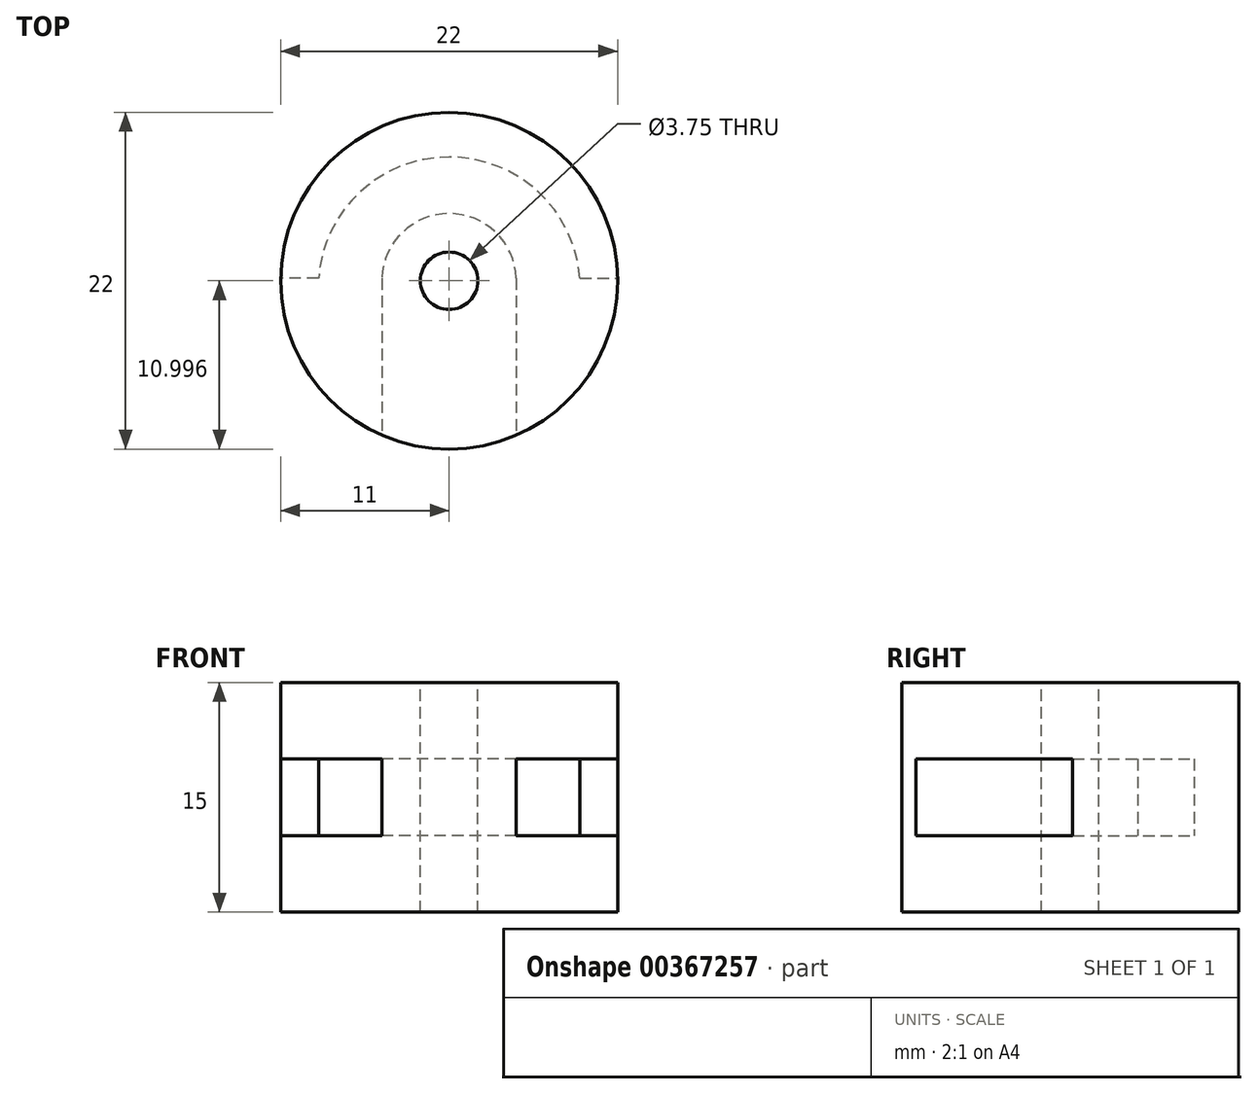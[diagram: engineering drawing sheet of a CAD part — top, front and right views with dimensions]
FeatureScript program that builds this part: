
annotation { "Feature Type Name" : "Feature", "Feature Type Description" : "" }
export const myFeature = defineFeature(function(context is Context, id is Id, definition is map)
    precondition{}
    {
        {
            var Q0;
            Q0=qCreatedBy(makeId("Top.planeOp"),FACE);
            var sketch = newSketch(context, id + "F0", { "sketchPlane" : qUnion([Q0])});
            skCircle(sketch, "E0", {"center": v(-55.33, -34.02) * mm, "radius": 11 * mm});
            skSolve(sketch);
        }
        {
            var Q0;
            Q0 = qSketchRegion(id + "F0", true);
            extrude(context, id + "F1", {"entities" : qUnion([Q0]), "depth" : 5 * mm});
        }
        {
            var Q0;
            Q0=makeQuery(id+"F1.opExtrude","CAP_FACE",FACE,{"disambiguationData":[OSD([sQuery(id+"F0.wireOp",EDGE,"E0")])],"isStart":false});
            var sketch = newSketch(context, id + "F2", { "sketchPlane" : qUnion([Q0])});
            skCircle(sketch, "E1", {"center": v(-55.33, -34.02) * mm, "radius": 11 * mm});
            skCircle(sketch, "E2", {"center": v(-55.33, -34.02) * mm, "radius": 1.88 * mm, "construction": true});
            skArc(sketch, "E3", {"start": v(-50.94, -34.18) * mm, "mid": v(-55.33, -29.63) * mm, "end": v(-59.72, -34.18) * mm});
            skArc(sketch, "E4", {"start": v(-46.8, -33.86) * mm, "mid": v(-55.33, -25.94) * mm, "end": v(-63.86, -33.86) * mm});
            skLineSegment(sketch, "E5", {"start": v(-50.94, -33.86) * mm, "end": v(-50.94, -44.11) * mm});
            skLineSegment(sketch, "E6", {"start": v(-59.72, -33.86) * mm, "end": v(-59.72, -44.11) * mm});
            skLineSegment(sketch, "E7", {"start": v(-63.86, -33.86) * mm, "end": v(-66.33, -33.86) * mm});
            skLineSegment(sketch, "E8", {"start": v(-46.8, -33.86) * mm, "end": v(-44.33, -33.86) * mm});
            skSolve(sketch);
        }
        {
            var Q0;
            Q0=makeQuery(id+"F2.imprint","IMPRINT",FACE,{"disambiguationData":[TD([[makeQuery(id+"F2.imprint","IMPRINT",EDGE,{"derivedFrom":sQuery(id+"F2.wireOp",EDGE,"E4")}),-1.0]])]});
            var Q1;
            {var subQ0=sQuery(id+"F2.wireOp",EDGE,"E5");var subQ3=sQuery(id+"F2.wireOp",EDGE,"E1");var subQ4=makeQuery(id+"F2.imprint","INTERSECT",VERTEX,{"derivedFrom":[subQ3,subQ0]});Q1=makeQuery(id+"F2.imprint","IMPRINT",FACE,{"disambiguationData":[TD([[makeQuery(id+"F2.imprint","IMPRINT",EDGE,{"disambiguationData":[TD([[subQ4,1.0]])],"derivedFrom":subQ3}),1.0]])]});}
            extrude(context, id + "F3", {"entities" : qUnion([Q0, Q1]), "operationType" : NewBodyOperationType.ADD, "depth" : 5 * mm});
        }
        {
            var Q0;
            Q0=makeQuery(id+"F3.opExtrude","CAP_FACE",FACE,{"disambiguationData":[OSD([sQuery(id+"F2.wireOp",EDGE,"E1"),sQuery(id+"F2.wireOp",EDGE,"E3"),sQuery(id+"F2.wireOp",EDGE,"E5"),sQuery(id+"F2.wireOp",EDGE,"E6")])],"isStart":false});
            var sketch = newSketch(context, id + "F4", { "sketchPlane" : qUnion([Q0])});
            skCircle(sketch, "E9", {"center": v(-55.33, -34.02) * mm, "radius": 11 * mm});
            skSolve(sketch);
        }
        {
            var Q0;
            Q0 = qSketchRegion(id + "F4", true);
            extrude(context, id + "F5", {"entities" : qUnion([Q0]), "operationType" : NewBodyOperationType.ADD, "depth" : 5 * mm});
        }
        {
            var Q0;
            Q0=makeQuery(id+"F5.opExtrude","CAP_FACE",FACE,{"disambiguationData":[OSD([sQuery(id+"F4.wireOp",EDGE,"E9")])],"isStart":false});
            var sketch = newSketch(context, id + "F6", { "sketchPlane" : qUnion([Q0])});
            skCircle(sketch, "E10", {"center": v(-55.33, -34.02) * mm, "radius": 1.88 * mm});
            skSolve(sketch);
        }
        {
            var Q0;
            Q0 = qSketchRegion(id + "F6", true);
            extrude(context, id + "F7", {"entities" : qUnion([Q0]), "operationType" : NewBodyOperationType.REMOVE, "oppositeDirection" : true, "depth" : 25 * mm});
        }
    });
